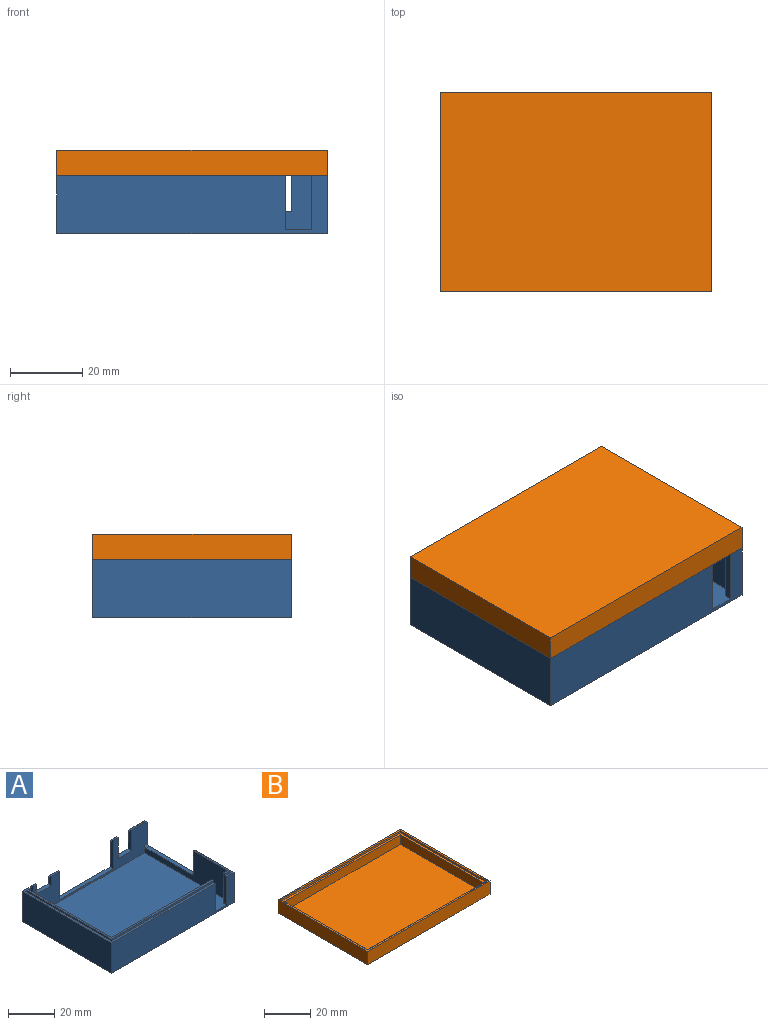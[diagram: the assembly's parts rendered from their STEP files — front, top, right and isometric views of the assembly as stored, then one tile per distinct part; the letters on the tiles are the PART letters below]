
ASSEMBLY  parts=2 mates=1
PART A: 51 faces, bbox 75x55x17 mm
  f0: plane 23x4.5mm, normal (0,0,1), area 29mm2, adj f2,f3,f23,f26,f45,f49
  f1: plane 21.9x3.4mm, normal (0,0,1), area 22mm2, adj f3,f4,f26,f32,f45,f49
  f2: plane 75x16mm, normal (0,-1,0), area 1095mm2, adj f0,f8,f22,f23,f24,f29,f49,f50
  f3: plane 3.4x1mm, normal (0,-1,0), area 3.4mm2, adj f0,f1,f26,f49
  f4: plane 16x2.5mm, normal (0,1,0), area 40mm2, adj f1,f29,f32,f49
  f5: plane 10x2mm, normal (0,0,1), area 12mm2, adj f7,f11,f15,f20,f23,f40
  f6: plane 8.9x0.9mm, normal (0,0,1), area 8mm2, adj f7,f15,f20,f40
  f7: plane 1x0.9mm, normal (1,0,0), area 0.9mm2, adj f5,f6,f15,f20
  f8: plane 63.5x55mm, normal (0,0,1), area 131.2mm2, adj f2,f11,f12,f24,f25,f28,f42,f50
  f9: plane 3x1.1mm, normal (0,0,1), area 3.3mm2, adj f11,f13,f37,f39
  f10: plane 5x1.1mm, normal (0,0,1), area 5.5mm2, adj f11,f14,f34,f36
  f11: plane 75x16mm, normal (0,1,0), area 614mm2, adj f5,f8,f9,f10,f21,f22,f23,f24
  f12: plane 1.9x1mm, normal (0,1,0), area 1.9mm2, adj f8,f16,f28,f42
  f13: plane 3x1mm, normal (0,1,0), area 3mm2, adj f9,f17,f37,f39
  f14: plane 5x1mm, normal (0,1,0), area 5mm2, adj f10,f18,f34,f36
  f15: plane 8.9x1mm, normal (0,1,0), area 8.9mm2, adj f5,f6,f7,f40
  f16: plane 62.4x52.8mm, normal (0,0,1), area 103.8mm2, adj f12,f20,f25,f28,f30,f31,f42,f50
  f17: plane 3x0.9mm, normal (0,0,1), area 2.7mm2, adj f13,f20,f37,f39
  f18: plane 5x0.9mm, normal (0,0,1), area 4.5mm2, adj f14,f20,f34,f36
  f19: plane 2x0.9mm, normal (0,0,1), area 1.8mm2, adj f20,f27,f33,f43
  f20: plane 73x16mm, normal (0,-1,0), area 520.9mm2, adj f5,f6,f7,f16,f17,f18,f19,f23
  f21: plane 2x1.1mm, normal (0,0,1), area 2.2mm2, adj f11,f27,f33,f43
  f22: plane 75x55mm, normal (0,0,-1), area 4125mm2, adj f2,f11,f23,f24
  f23: plane 55x16mm, normal (1,0,0), area 520.4mm2, adj f0,f2,f5,f11,f20,f22,f45,f46
  f24: plane 55x16mm, normal (-1,0,0), area 880mm2, adj f2,f8,f11,f22
  f25: plane 62.4x1mm, normal (0,-1,0), area 62.4mm2, adj f8,f16,f28,f50
  f26: plane 21.9x1mm, normal (1,0,0), area 21.9mm2, adj f0,f1,f3,f45
  f27: plane 2x1mm, normal (0,1,0), area 2mm2, adj f19,f21,f33,f43
  f28: plane 52.8x1mm, normal (-1,0,0), area 52.8mm2, adj f8,f12,f16,f25
  f29: plane 71x53mm, normal (0,0,1), area 3635mm2, adj f2,f4,f20,f30,f31,f32,f49,f50
  f30: plane 51x16mm, normal (1,0,0), area 816mm2, adj f16,f20,f29,f31
  f31: plane 61.5x16mm, normal (0,1,0), area 984mm2, adj f16,f29,f30,f50
  f32: plane 51x16mm, normal (-1,0,0), area 426.4mm2, adj f1,f4,f20,f29,f45,f46,f47,f48
  f33: plane 5x2mm, normal (1,0,0), area 8.9mm2, adj f11,f19,f20,f21,f27,f35
  f34: plane 5x2mm, normal (-1,0,0), area 8.9mm2, adj f10,f11,f14,f18,f20,f35
  f35: plane 9x2mm, normal (0,0,1), area 18mm2, adj f11,f20,f33,f34
  f36: plane 15x2mm, normal (1,0,0), area 28.9mm2, adj f10,f11,f14,f18,f20,f38
  f37: plane 15x2mm, normal (-1,0,0), area 28.9mm2, adj f9,f11,f13,f17,f20,f38
  f38: plane 33x2mm, normal (0,0,1), area 66mm2, adj f11,f20,f36,f37
  f39: plane 11x2mm, normal (1,0,0), area 20.9mm2, adj f9,f11,f13,f17,f20,f41
  f40: plane 11x2mm, normal (-1,0,0), area 20.9mm2, adj f5,f6,f11,f15,f20,f41
  f41: plane 8x2mm, normal (0,0,1), area 16mm2, adj f11,f20,f39,f40
  f42: plane 5x2mm, normal (1,0,0), area 8.9mm2, adj f8,f11,f12,f16,f20,f44
  f43: plane 5x2mm, normal (-1,0,0), area 8.9mm2, adj f11,f19,f20,f21,f27,f44
  f44: plane 2x2mm, normal (0,0,1), area 4mm2, adj f11,f20,f42,f43
  f45: plane 12x2mm, normal (0,1,0), area 22.9mm2, adj f0,f1,f23,f26,f32,f46
  f46: cylinder r=1mm len=2mm, axis (1,0,0), area 3.1mm2, adj f23,f32,f45,f47
  f47: plane 28x2mm, normal (0,0,1), area 56mm2, adj f23,f32,f46,f48
  f48: cylinder r=1mm len=2mm, axis (1,0,0), area 3.1mm2, adj f20,f23,f32,f47
  f49: plane 16x2mm, normal (-1,0,0), area 30.9mm2, adj f0,f1,f2,f3,f4,f29
  f50: plane 16x2mm, normal (1,0,0), area 30.9mm2, adj f2,f8,f16,f25,f29,f31
PART B: 16 faces, bbox 75x55x7 mm
  f0: plane 75x55mm, normal (0,0,1), area 230.8mm2, adj f2,f3,f4,f5,f6,f7,f8,f9
  f1: plane 75x55mm, normal (0,0,-1), area 4125mm2, adj f2,f3,f4,f5
  f2: plane 75x7mm, normal (0,-1,0), area 525mm2, adj f0,f1,f3,f5
  f3: plane 55x7mm, normal (1,0,0), area 385mm2, adj f0,f1,f2,f4
  f4: plane 75x7mm, normal (0,1,0), area 525mm2, adj f0,f1,f3,f5
  f5: plane 55x7mm, normal (-1,0,0), area 385mm2, adj f0,f1,f2,f4
  f6: plane 73.2x1mm, normal (0,1,0), area 73.2mm2, adj f0,f7,f9,f10
  f7: plane 53.2x1mm, normal (-1,0,0), area 53.2mm2, adj f0,f6,f8,f10
  f8: plane 73.2x1mm, normal (0,-1,0), area 73.2mm2, adj f0,f7,f9,f10
  f9: plane 53.2x1mm, normal (1,0,0), area 53.2mm2, adj f0,f6,f8,f10
  f10: plane 73.2x53.2mm, normal (0,0,1), area 273.2mm2, adj f6,f7,f8,f9,f12,f13,f14,f15
  f11: plane 71x51mm, normal (0,0,1), area 3621mm2, adj f12,f13,f14,f15
  f12: plane 51x5mm, normal (1,0,0), area 255mm2, adj f10,f11,f13,f15
  f13: plane 71x5mm, normal (0,-1,0), area 355mm2, adj f10,f11,f12,f14
  f14: plane 51x5mm, normal (-1,0,0), area 255mm2, adj f10,f11,f13,f15
  f15: plane 71x5mm, normal (0,1,0), area 355mm2, adj f10,f11,f12,f14
PLACE A t=(-0.22,9.95,15.11)mm
PLACE B rot(axis=(1,0,0),180deg) t=(-0.22,9.95,38.11)mm
MATE fastened B.f0 <-> A.f0  axis (0,0,-1) through (37.28,-17.55,31.11)mm
